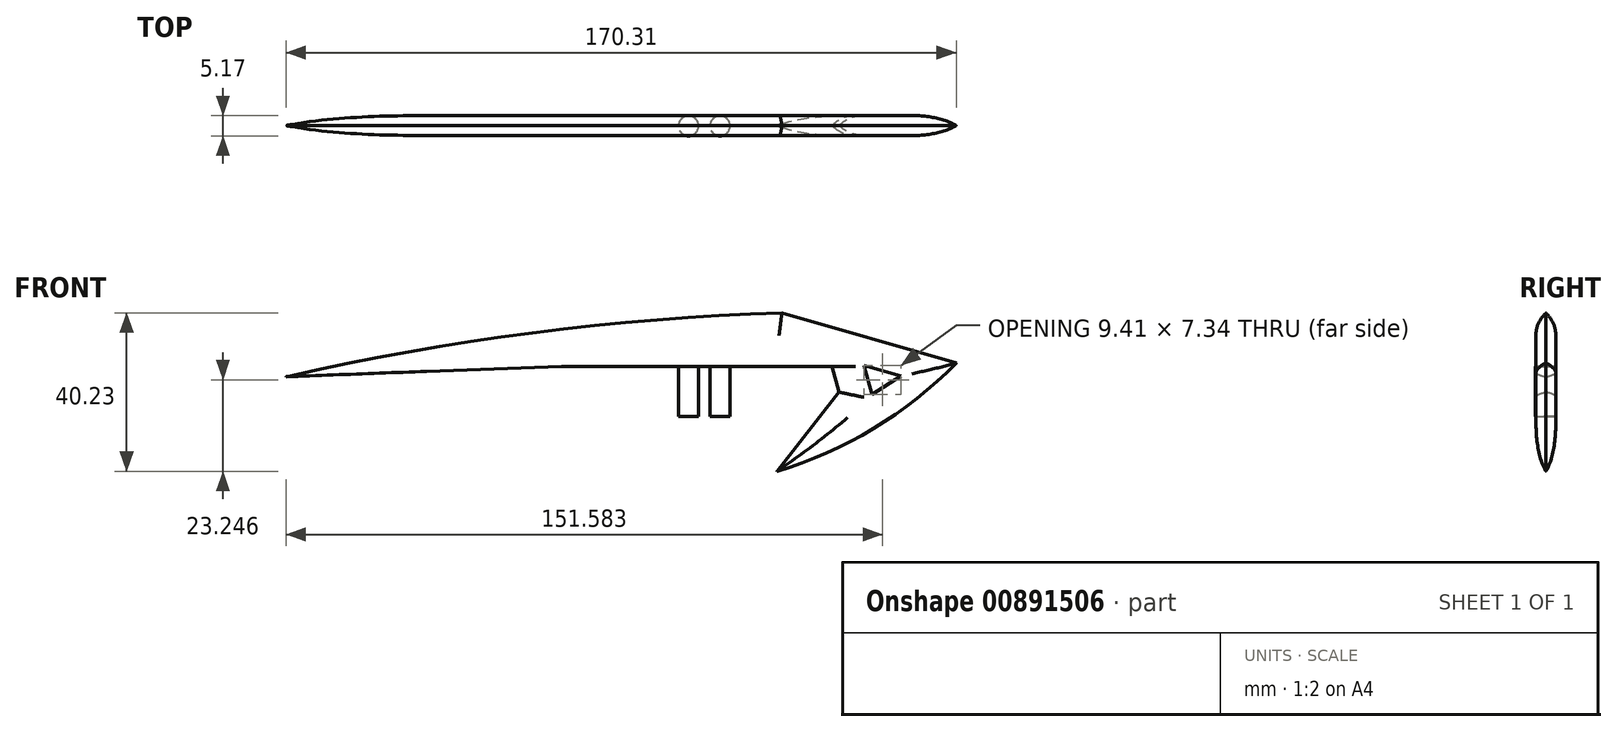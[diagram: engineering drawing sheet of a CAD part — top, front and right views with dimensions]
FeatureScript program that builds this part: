
annotation { "Feature Type Name" : "Feature", "Feature Type Description" : "" }
export const myFeature = defineFeature(function(context is Context, id is Id, definition is map)
    precondition{}
    {
        {
            var Q0;
            Q0=qCreatedBy(makeId("Top.planeOp"),FACE);
            var sketch = newSketch(context, id + "F0", { "sketchPlane" : qUnion([Q0])});
            skCircle(sketch, "E0", {"center": v(-29.33, -4.66) * mm, "radius": 2.54 * mm});
            skCircle(sketch, "E1", {"center": v(-21.33, -4.66) * mm, "radius": 2.54 * mm});
            skSolve(sketch);
        }
        {
            var Q0;
            Q0 = qSketchRegion(id + "F0", true);
            extrude(context, id + "F1", {"entities" : qUnion([Q0]), "depth" : 12.7 * mm, "offsetDistance" : 25.4 * mm});
        }
        {
            var Q0;
            Q0=qCreatedBy(makeId("Front.planeOp"),FACE);
            var sketch = newSketch(context, id + "F2", { "sketchPlane" : qUnion([Q0])});
            skLineSegment(sketch, "E2", {"start": v(-61.62, 12.7) * mm, "end": v(7.17, 12.7) * mm});
            skLineSegment(sketch, "E3", {"start": v(7.17, 12.7) * mm, "end": v(8.94, 6.12) * mm});
            skLineSegment(sketch, "E4", {"start": v(8.94, 6.12) * mm, "end": v(-6.9, -14) * mm});
            skLineSegment(sketch, "E5", {"start": v(38.7, 13.48) * mm, "end": v(-5.62, 26.23) * mm});
            skLineSegment(sketch, "E6", {"start": v(-131.6, 10.04) * mm, "end": v(-61.62, 12.7) * mm});
            skArc(sketch, "E7", {"start": v(-6.9, -14) * mm, "mid": v(17.64, -3.15) * mm, "end": v(38.7, 13.48) * mm});
            skArc(sketch, "E8", {"start": v(-5.62, 26.23) * mm, "mid": v(-69, 21.2) * mm, "end": v(-131.6, 10.04) * mm});
            skSolve(sketch);
        }
        {
            var Q0;
            Q0 = qSketchRegion(id + "F2", true);
            extrude(context, id + "F3", {"entities" : qUnion([Q0]), "endBound" : BoundingType.SYMMETRIC, "depth" : 5.08 * mm, "offsetDistance" : 25.4 * mm});
        }
        {
            var Q0;
            Q0=makeQuery(id+"F3.opExtrude","CAP_EDGE",EDGE,{"disambiguationData":[OSD([sQuery(id+"F2.wireOp",EDGE,"E4")])],"isStart":false});
            var Q1;
            Q1=makeQuery(id+"F3.opExtrude","CAP_EDGE",EDGE,{"disambiguationData":[OSD([sQuery(id+"F2.wireOp",EDGE,"E7")])],"isStart":false});
            var Q2;
            Q2=makeQuery(id+"F3.opExtrude","CAP_EDGE",EDGE,{"disambiguationData":[OSD([sQuery(id+"F2.wireOp",EDGE,"E3")])],"isStart":false});
            var Q3;
            Q3=makeQuery(id+"F3.opExtrude","CAP_EDGE",EDGE,{"disambiguationData":[OSD([sQuery(id+"F2.wireOp",EDGE,"E3")])],"isStart":true});
            var Q4;
            Q4=makeQuery(id+"F3.opExtrude","CAP_EDGE",EDGE,{"disambiguationData":[OSD([sQuery(id+"F2.wireOp",EDGE,"E4")])],"isStart":true});
            var Q5;
            Q5=makeQuery(id+"F3.opExtrude","CAP_EDGE",EDGE,{"disambiguationData":[OSD([sQuery(id+"F2.wireOp",EDGE,"E7")])],"isStart":true});
            var Q6;
            Q6=makeQuery(id+"F3.opExtrude","CAP_EDGE",EDGE,{"disambiguationData":[OSD([sQuery(id+"F2.wireOp",EDGE,"E5")])],"isStart":true});
            var Q7;
            Q7=makeQuery(id+"F3.opExtrude","CAP_EDGE",EDGE,{"disambiguationData":[OSD([sQuery(id+"F2.wireOp",EDGE,"E5")])],"isStart":false});
            chamfer(context, id + "F4", {"entities" : qUnion([Q0, Q1, Q2, Q3, Q4, Q5, Q6, Q7]), "chamferType" : ChamferType.OFFSET_ANGLE, "width" : 2.54 * mm, "oppositeDirection" : false, "angle" : 45 * degree, "tangentPropagation" : true});
        }
        {
            var Q0;
            Q0=makeQuery(id+"F3.opExtrude","CAP_EDGE",EDGE,{"disambiguationData":[OSD([sQuery(id+"F2.wireOp",EDGE,"E8")])],"isStart":false});
            var Q1;
            Q1=makeQuery(id+"F3.opExtrude","CAP_EDGE",EDGE,{"disambiguationData":[OSD([sQuery(id+"F2.wireOp",EDGE,"E8")])],"isStart":true});
            chamfer(context, id + "F5", {"entities" : qUnion([Q0, Q1]), "width" : 2.54 * mm, "tangentPropagation" : true});
        }
        {
            var Q0;
            {var subQ0=sQuery(id+"F2.wireOp",EDGE,"E3");Q0=makeQuery(id+"F4.opChamfer","BLEND_EDGE",EDGE,{"blendedFrom":[makeQuery(id+"F3.opExtrude","CAP_EDGE",EDGE,{"disambiguationData":[OSD([subQ0])],"isStart":false}),makeQuery(id+"F3.opExtrude","CAP_FACE",FACE,{"disambiguationData":[OSD([sQuery(id+"F2.wireOp",EDGE,"E2"),subQ0,sQuery(id+"F2.wireOp",EDGE,"E4"),sQuery(id+"F2.wireOp",EDGE,"E5"),sQuery(id+"F2.wireOp",EDGE,"E6"),sQuery(id+"F2.wireOp",EDGE,"E7"),sQuery(id+"F2.wireOp",EDGE,"E8")])],"isStart":false})],"blendedInto":[makeQuery(id+"F3.opExtrude","CAP_FACE",FACE,{"disambiguationData":[OSD([sQuery(id+"F2.wireOp",EDGE,"E2"),subQ0,sQuery(id+"F2.wireOp",EDGE,"E4"),sQuery(id+"F2.wireOp",EDGE,"E5"),sQuery(id+"F2.wireOp",EDGE,"E6"),sQuery(id+"F2.wireOp",EDGE,"E7"),sQuery(id+"F2.wireOp",EDGE,"E8")])],"isStart":false})]});}
            var Q1;
            {var subQ0=sQuery(id+"F2.wireOp",EDGE,"E4");Q1=makeQuery(id+"F4.opChamfer","BLEND_EDGE",EDGE,{"blendedFrom":[makeQuery(id+"F3.opExtrude","CAP_EDGE",EDGE,{"disambiguationData":[OSD([subQ0])],"isStart":false}),makeQuery(id+"F3.opExtrude","CAP_FACE",FACE,{"disambiguationData":[OSD([sQuery(id+"F2.wireOp",EDGE,"E2"),sQuery(id+"F2.wireOp",EDGE,"E3"),subQ0,sQuery(id+"F2.wireOp",EDGE,"E5"),sQuery(id+"F2.wireOp",EDGE,"E6"),sQuery(id+"F2.wireOp",EDGE,"E7"),sQuery(id+"F2.wireOp",EDGE,"E8")])],"isStart":false})],"blendedInto":[makeQuery(id+"F3.opExtrude","CAP_FACE",FACE,{"disambiguationData":[OSD([sQuery(id+"F2.wireOp",EDGE,"E2"),sQuery(id+"F2.wireOp",EDGE,"E3"),subQ0,sQuery(id+"F2.wireOp",EDGE,"E5"),sQuery(id+"F2.wireOp",EDGE,"E6"),sQuery(id+"F2.wireOp",EDGE,"E7"),sQuery(id+"F2.wireOp",EDGE,"E8")])],"isStart":false})]});}
            var Q2;
            {var subQ0=sQuery(id+"F2.wireOp",EDGE,"E7");Q2=makeQuery(id+"F4.opChamfer","BLEND_EDGE",EDGE,{"blendedFrom":[makeQuery(id+"F3.opExtrude","CAP_EDGE",EDGE,{"disambiguationData":[OSD([subQ0])],"isStart":false}),makeQuery(id+"F3.opExtrude","CAP_FACE",FACE,{"disambiguationData":[OSD([sQuery(id+"F2.wireOp",EDGE,"E2"),sQuery(id+"F2.wireOp",EDGE,"E3"),sQuery(id+"F2.wireOp",EDGE,"E4"),sQuery(id+"F2.wireOp",EDGE,"E5"),sQuery(id+"F2.wireOp",EDGE,"E6"),subQ0,sQuery(id+"F2.wireOp",EDGE,"E8")])],"isStart":false})],"blendedInto":[makeQuery(id+"F3.opExtrude","CAP_FACE",FACE,{"disambiguationData":[OSD([sQuery(id+"F2.wireOp",EDGE,"E2"),sQuery(id+"F2.wireOp",EDGE,"E3"),sQuery(id+"F2.wireOp",EDGE,"E4"),sQuery(id+"F2.wireOp",EDGE,"E5"),sQuery(id+"F2.wireOp",EDGE,"E6"),subQ0,sQuery(id+"F2.wireOp",EDGE,"E8")])],"isStart":false})]});}
            var Q3;
            {var subQ0=sQuery(id+"F2.wireOp",EDGE,"E5");Q3=makeQuery(id+"F4.opChamfer","BLEND_EDGE",EDGE,{"blendedFrom":[makeQuery(id+"F3.opExtrude","CAP_EDGE",EDGE,{"disambiguationData":[OSD([subQ0])],"isStart":false}),makeQuery(id+"F3.opExtrude","CAP_FACE",FACE,{"disambiguationData":[OSD([sQuery(id+"F2.wireOp",EDGE,"E2"),sQuery(id+"F2.wireOp",EDGE,"E3"),sQuery(id+"F2.wireOp",EDGE,"E4"),subQ0,sQuery(id+"F2.wireOp",EDGE,"E6"),sQuery(id+"F2.wireOp",EDGE,"E7"),sQuery(id+"F2.wireOp",EDGE,"E8")])],"isStart":false})],"blendedInto":[makeQuery(id+"F3.opExtrude","CAP_FACE",FACE,{"disambiguationData":[OSD([sQuery(id+"F2.wireOp",EDGE,"E2"),sQuery(id+"F2.wireOp",EDGE,"E3"),sQuery(id+"F2.wireOp",EDGE,"E4"),subQ0,sQuery(id+"F2.wireOp",EDGE,"E6"),sQuery(id+"F2.wireOp",EDGE,"E7"),sQuery(id+"F2.wireOp",EDGE,"E8")])],"isStart":false})]});}
            var Q4;
            {var subQ0=sQuery(id+"F2.wireOp",EDGE,"E8");Q4=makeQuery(id+"F5.opChamfer","BLEND_EDGE",EDGE,{"blendedFrom":[makeQuery(id+"F3.opExtrude","CAP_EDGE",EDGE,{"disambiguationData":[OSD([subQ0])],"isStart":false}),makeQuery(id+"F3.opExtrude","CAP_FACE",FACE,{"disambiguationData":[OSD([sQuery(id+"F2.wireOp",EDGE,"E2"),sQuery(id+"F2.wireOp",EDGE,"E3"),sQuery(id+"F2.wireOp",EDGE,"E4"),sQuery(id+"F2.wireOp",EDGE,"E5"),sQuery(id+"F2.wireOp",EDGE,"E6"),sQuery(id+"F2.wireOp",EDGE,"E7"),subQ0])],"isStart":false})],"blendedInto":[makeQuery(id+"F3.opExtrude","CAP_FACE",FACE,{"disambiguationData":[OSD([sQuery(id+"F2.wireOp",EDGE,"E2"),sQuery(id+"F2.wireOp",EDGE,"E3"),sQuery(id+"F2.wireOp",EDGE,"E4"),sQuery(id+"F2.wireOp",EDGE,"E5"),sQuery(id+"F2.wireOp",EDGE,"E6"),sQuery(id+"F2.wireOp",EDGE,"E7"),subQ0])],"isStart":false})]});}
            var Q5;
            {var subQ0=sQuery(id+"F2.wireOp",EDGE,"E3");Q5=makeQuery(id+"F4.opChamfer","BLEND_EDGE",EDGE,{"blendedFrom":[makeQuery(id+"F3.opExtrude","CAP_EDGE",EDGE,{"disambiguationData":[OSD([subQ0])],"isStart":true}),makeQuery(id+"F3.opExtrude","CAP_FACE",FACE,{"disambiguationData":[OSD([sQuery(id+"F2.wireOp",EDGE,"E2"),subQ0,sQuery(id+"F2.wireOp",EDGE,"E4"),sQuery(id+"F2.wireOp",EDGE,"E5"),sQuery(id+"F2.wireOp",EDGE,"E6"),sQuery(id+"F2.wireOp",EDGE,"E7"),sQuery(id+"F2.wireOp",EDGE,"E8")])],"isStart":true})],"blendedInto":[makeQuery(id+"F3.opExtrude","CAP_FACE",FACE,{"disambiguationData":[OSD([sQuery(id+"F2.wireOp",EDGE,"E2"),subQ0,sQuery(id+"F2.wireOp",EDGE,"E4"),sQuery(id+"F2.wireOp",EDGE,"E5"),sQuery(id+"F2.wireOp",EDGE,"E6"),sQuery(id+"F2.wireOp",EDGE,"E7"),sQuery(id+"F2.wireOp",EDGE,"E8")])],"isStart":true})]});}
            var Q6;
            {var subQ0=sQuery(id+"F2.wireOp",EDGE,"E4");Q6=makeQuery(id+"F4.opChamfer","BLEND_EDGE",EDGE,{"blendedFrom":[makeQuery(id+"F3.opExtrude","CAP_EDGE",EDGE,{"disambiguationData":[OSD([subQ0])],"isStart":true}),makeQuery(id+"F3.opExtrude","CAP_FACE",FACE,{"disambiguationData":[OSD([sQuery(id+"F2.wireOp",EDGE,"E2"),sQuery(id+"F2.wireOp",EDGE,"E3"),subQ0,sQuery(id+"F2.wireOp",EDGE,"E5"),sQuery(id+"F2.wireOp",EDGE,"E6"),sQuery(id+"F2.wireOp",EDGE,"E7"),sQuery(id+"F2.wireOp",EDGE,"E8")])],"isStart":true})],"blendedInto":[makeQuery(id+"F3.opExtrude","CAP_FACE",FACE,{"disambiguationData":[OSD([sQuery(id+"F2.wireOp",EDGE,"E2"),sQuery(id+"F2.wireOp",EDGE,"E3"),subQ0,sQuery(id+"F2.wireOp",EDGE,"E5"),sQuery(id+"F2.wireOp",EDGE,"E6"),sQuery(id+"F2.wireOp",EDGE,"E7"),sQuery(id+"F2.wireOp",EDGE,"E8")])],"isStart":true})]});}
            var Q7;
            {var subQ0=sQuery(id+"F2.wireOp",EDGE,"E7");Q7=makeQuery(id+"F4.opChamfer","BLEND_EDGE",EDGE,{"blendedFrom":[makeQuery(id+"F3.opExtrude","CAP_EDGE",EDGE,{"disambiguationData":[OSD([subQ0])],"isStart":true}),makeQuery(id+"F3.opExtrude","CAP_FACE",FACE,{"disambiguationData":[OSD([sQuery(id+"F2.wireOp",EDGE,"E2"),sQuery(id+"F2.wireOp",EDGE,"E3"),sQuery(id+"F2.wireOp",EDGE,"E4"),sQuery(id+"F2.wireOp",EDGE,"E5"),sQuery(id+"F2.wireOp",EDGE,"E6"),subQ0,sQuery(id+"F2.wireOp",EDGE,"E8")])],"isStart":true})],"blendedInto":[makeQuery(id+"F3.opExtrude","CAP_FACE",FACE,{"disambiguationData":[OSD([sQuery(id+"F2.wireOp",EDGE,"E2"),sQuery(id+"F2.wireOp",EDGE,"E3"),sQuery(id+"F2.wireOp",EDGE,"E4"),sQuery(id+"F2.wireOp",EDGE,"E5"),sQuery(id+"F2.wireOp",EDGE,"E6"),subQ0,sQuery(id+"F2.wireOp",EDGE,"E8")])],"isStart":true})]});}
            var Q8;
            {var subQ0=sQuery(id+"F2.wireOp",EDGE,"E5");Q8=makeQuery(id+"F4.opChamfer","BLEND_EDGE",EDGE,{"blendedFrom":[makeQuery(id+"F3.opExtrude","CAP_EDGE",EDGE,{"disambiguationData":[OSD([subQ0])],"isStart":true}),makeQuery(id+"F3.opExtrude","CAP_FACE",FACE,{"disambiguationData":[OSD([sQuery(id+"F2.wireOp",EDGE,"E2"),sQuery(id+"F2.wireOp",EDGE,"E3"),sQuery(id+"F2.wireOp",EDGE,"E4"),subQ0,sQuery(id+"F2.wireOp",EDGE,"E6"),sQuery(id+"F2.wireOp",EDGE,"E7"),sQuery(id+"F2.wireOp",EDGE,"E8")])],"isStart":true})],"blendedInto":[makeQuery(id+"F3.opExtrude","CAP_FACE",FACE,{"disambiguationData":[OSD([sQuery(id+"F2.wireOp",EDGE,"E2"),sQuery(id+"F2.wireOp",EDGE,"E3"),sQuery(id+"F2.wireOp",EDGE,"E4"),subQ0,sQuery(id+"F2.wireOp",EDGE,"E6"),sQuery(id+"F2.wireOp",EDGE,"E7"),sQuery(id+"F2.wireOp",EDGE,"E8")])],"isStart":true})]});}
            var Q9;
            {var subQ0=sQuery(id+"F2.wireOp",EDGE,"E8");Q9=makeQuery(id+"F5.opChamfer","BLEND_EDGE",EDGE,{"blendedFrom":[makeQuery(id+"F3.opExtrude","CAP_EDGE",EDGE,{"disambiguationData":[OSD([subQ0])],"isStart":true}),makeQuery(id+"F3.opExtrude","CAP_FACE",FACE,{"disambiguationData":[OSD([sQuery(id+"F2.wireOp",EDGE,"E2"),sQuery(id+"F2.wireOp",EDGE,"E3"),sQuery(id+"F2.wireOp",EDGE,"E4"),sQuery(id+"F2.wireOp",EDGE,"E5"),sQuery(id+"F2.wireOp",EDGE,"E6"),sQuery(id+"F2.wireOp",EDGE,"E7"),subQ0])],"isStart":true})],"blendedInto":[makeQuery(id+"F3.opExtrude","CAP_FACE",FACE,{"disambiguationData":[OSD([sQuery(id+"F2.wireOp",EDGE,"E2"),sQuery(id+"F2.wireOp",EDGE,"E3"),sQuery(id+"F2.wireOp",EDGE,"E4"),sQuery(id+"F2.wireOp",EDGE,"E5"),sQuery(id+"F2.wireOp",EDGE,"E6"),sQuery(id+"F2.wireOp",EDGE,"E7"),subQ0])],"isStart":true})]});}
            fillet(context, id + "F6", {"entities" : qUnion([Q0, Q1, Q2, Q3, Q4, Q5, Q6, Q7, Q8, Q9]), "radius" : 7.62 * mm, "tangentPropagation" : true, "allowEdgeOverflow" : false});
        }
        {
            var Q0;
            Q0=makeQuery(id+"F1.opExtrude","SWEPT_BODY",BODY,{"disambiguationData":[OSD([sQuery(id+"F0.wireOp",EDGE,"E0")])]});
            var Q1;
            Q1=makeQuery(id+"F1.opExtrude","SWEPT_BODY",BODY,{"disambiguationData":[OSD([sQuery(id+"F0.wireOp",EDGE,"E1")])]});
            var Q2;
            Q2=qCreatedBy(makeId("Front.planeOp"),FACE);
            transform(context, id + "F7", {"entities" : qUnion([Q0, Q1]), "transformType" : TransformType.TRANSLATION_DISTANCE, "transformDirection" : qUnion([Q2]), "distance" : 4.57 * mm, "oppositeDirection" : true, "makeCopy" : false});
        }
        {
            var Q0;
            Q0=makeQuery(id+"F3.opExtrude","CAP_FACE",FACE,{"disambiguationData":[OSD([sQuery(id+"F2.wireOp",EDGE,"E2"),sQuery(id+"F2.wireOp",EDGE,"E3"),sQuery(id+"F2.wireOp",EDGE,"E4"),sQuery(id+"F2.wireOp",EDGE,"E5"),sQuery(id+"F2.wireOp",EDGE,"E6"),sQuery(id+"F2.wireOp",EDGE,"E7"),sQuery(id+"F2.wireOp",EDGE,"E8")])],"isStart":true});
            var sketch = newSketch(context, id + "F8", { "sketchPlane" : qUnion([Q0])});
            skLineSegment(sketch, "E9", {"start": v(-27.41, 10.8) * mm, "end": v(6.33, 20.5) * mm});
            skArc(sketch, "E10", {"start": v(95.86, 11.4) * mm, "mid": v(51.24, 17.37) * mm, "end": v(6.33, 20.5) * mm});
            skArc(sketch, "E11", {"start": v(-27.41, 10.8) * mm, "mid": v(-19.45, 4.97) * mm, "end": v(-11.11, -0.33) * mm});
            skLineSegment(sketch, "E12", {"start": v(-11.11, -0.33) * mm, "end": v(-15.19, 4.84) * mm});
            skLineSegment(sketch, "E13", {"start": v(-15.19, 4.84) * mm, "end": v(-13.07, 12.7) * mm});
            skLineSegment(sketch, "E14", {"start": v(-13.07, 12.7) * mm, "end": v(61.62, 12.7) * mm});
            skLineSegment(sketch, "E15", {"start": v(61.62, 12.7) * mm, "end": v(95.86, 11.4) * mm});
            skLineSegment(sketch, "E16", {"start": v(-15.27, 12.92) * mm, "end": v(-24.68, 10.21) * mm});
            skLineSegment(sketch, "E17", {"start": v(-24.68, 10.21) * mm, "end": v(-17.24, 5.57) * mm});
            skLineSegment(sketch, "E18", {"start": v(-17.24, 5.57) * mm, "end": v(-15.27, 12.92) * mm});
            skSolve(sketch);
        }
        {
            var Q0;
            Q0=makeQuery(id+"F8.imprint","IMPRINT",FACE,{"disambiguationData":[TD([[makeQuery(id+"F8.imprint","IMPRINT",EDGE,{"derivedFrom":sQuery(id+"F8.wireOp",EDGE,"E16")}),1.0]])]});
            extrude(context, id + "F9", {"entities" : qUnion([Q0]), "operationType" : NewBodyOperationType.REMOVE, "oppositeDirection" : true, "depth" : 7.62 * mm, "offsetDistance" : 25.4 * mm});
        }
    });
